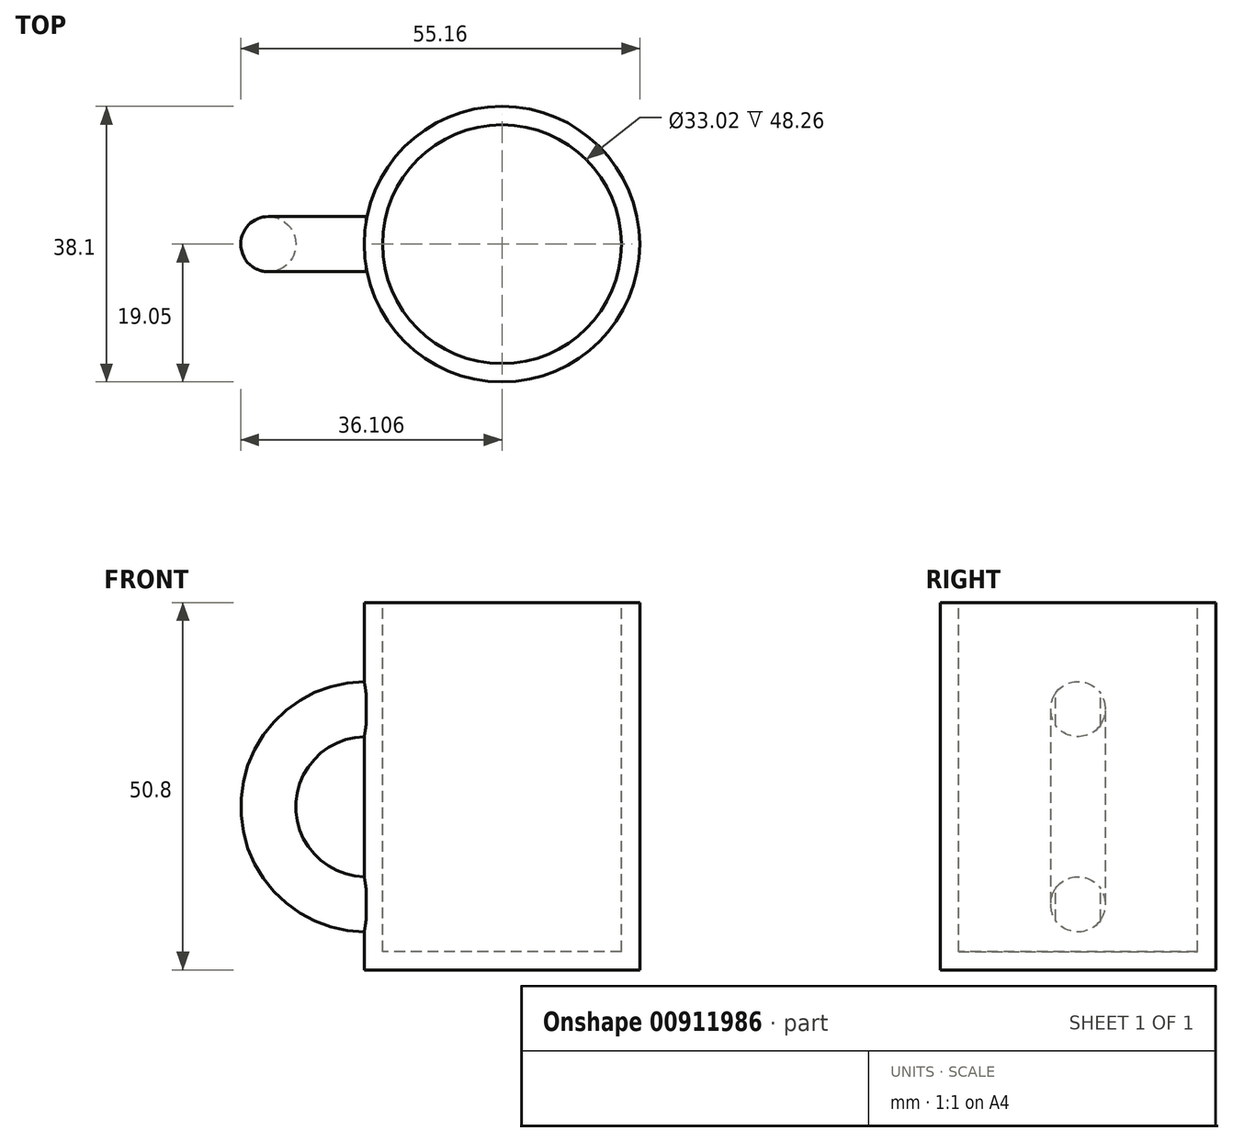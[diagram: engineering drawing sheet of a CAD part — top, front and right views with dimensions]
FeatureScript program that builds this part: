
annotation { "Feature Type Name" : "Feature", "Feature Type Description" : "" }
export const myFeature = defineFeature(function(context is Context, id is Id, definition is map)
    precondition{}
    {
        {
            var Q0;
            Q0=qCreatedBy(makeId("Front.planeOp"),FACE);
            var sketch = newSketch(context, id + "F0", { "sketchPlane" : qUnion([Q0])});
            skLineSegment(sketch, "E0.bottom", {"start": v(18.8, 55.32) * mm, "end": v(37.85, 55.32) * mm});
            skLineSegment(sketch, "E0.top", {"start": v(18.8, 4.52) * mm, "end": v(37.85, 4.52) * mm});
            skLineSegment(sketch, "E0.left", {"start": v(18.8, 55.32) * mm, "end": v(18.8, 4.52) * mm});
            skLineSegment(sketch, "E0.right", {"start": v(37.85, 55.32) * mm, "end": v(37.85, 4.52) * mm});
            skLineSegment(sketch, "E1", {"start": v(18.8, 55.32) * mm, "end": v(0, 55.32) * mm});
            skSolve(sketch);
        }
        {
            var Q0;
            Q0 = qSketchRegion(id + "F0", true);
            var Q1;
            Q1=sQuery(id+"F0.wireOp",EDGE,"E0.left");
            revolve(context, id + "F1", {"surfaceOperationType" : NewSurfaceOperationType.NEW, "entities" : qUnion([Q0]), "axis" : qUnion([Q1]), "revolveType" : RevolveType.FULL});
        }
        {
            var Q0;
            Q0=makeQuery(id+"F1.opRevolve","SWEPT_FACE",FACE,{"disambiguationData":[OSD([sQuery(id+"F0.wireOp",EDGE,"E0.bottom")])]});
            shell(context, id + "F2", {"entities" : qUnion([Q0]), "thickness" : 2.54 * mm});
        }
        {
            var Q0;
            Q0=qCreatedBy(makeId("Right.planeOp"),FACE);
            var sketch = newSketch(context, id + "F3", { "sketchPlane" : qUnion([Q0])});
            skCircle(sketch, "E2", {"center": v(0, 13.58) * mm, "radius": 3.81 * mm});
            skLineSegment(sketch, "E3", {"start": v(3.45, 27.08) * mm, "end": v(-4.49, 27.08) * mm, "construction": true});
            skSolve(sketch);
        }
        {
            var Q0;
            Q0 = qSketchRegion(id + "F3", true);
            var Q1;
            Q1=sQuery(id+"F3.wireOp",EDGE,"E3");
            revolve(context, id + "F4", {"operationType" : NewBodyOperationType.ADD, "surfaceOperationType" : NewSurfaceOperationType.NEW, "entities" : qUnion([Q0]), "axis" : qUnion([Q1]), "revolveType" : RevolveType.ONE_DIRECTION, "oppositeDirection" : true, "angle" : 180 * degree});
        }
    });
